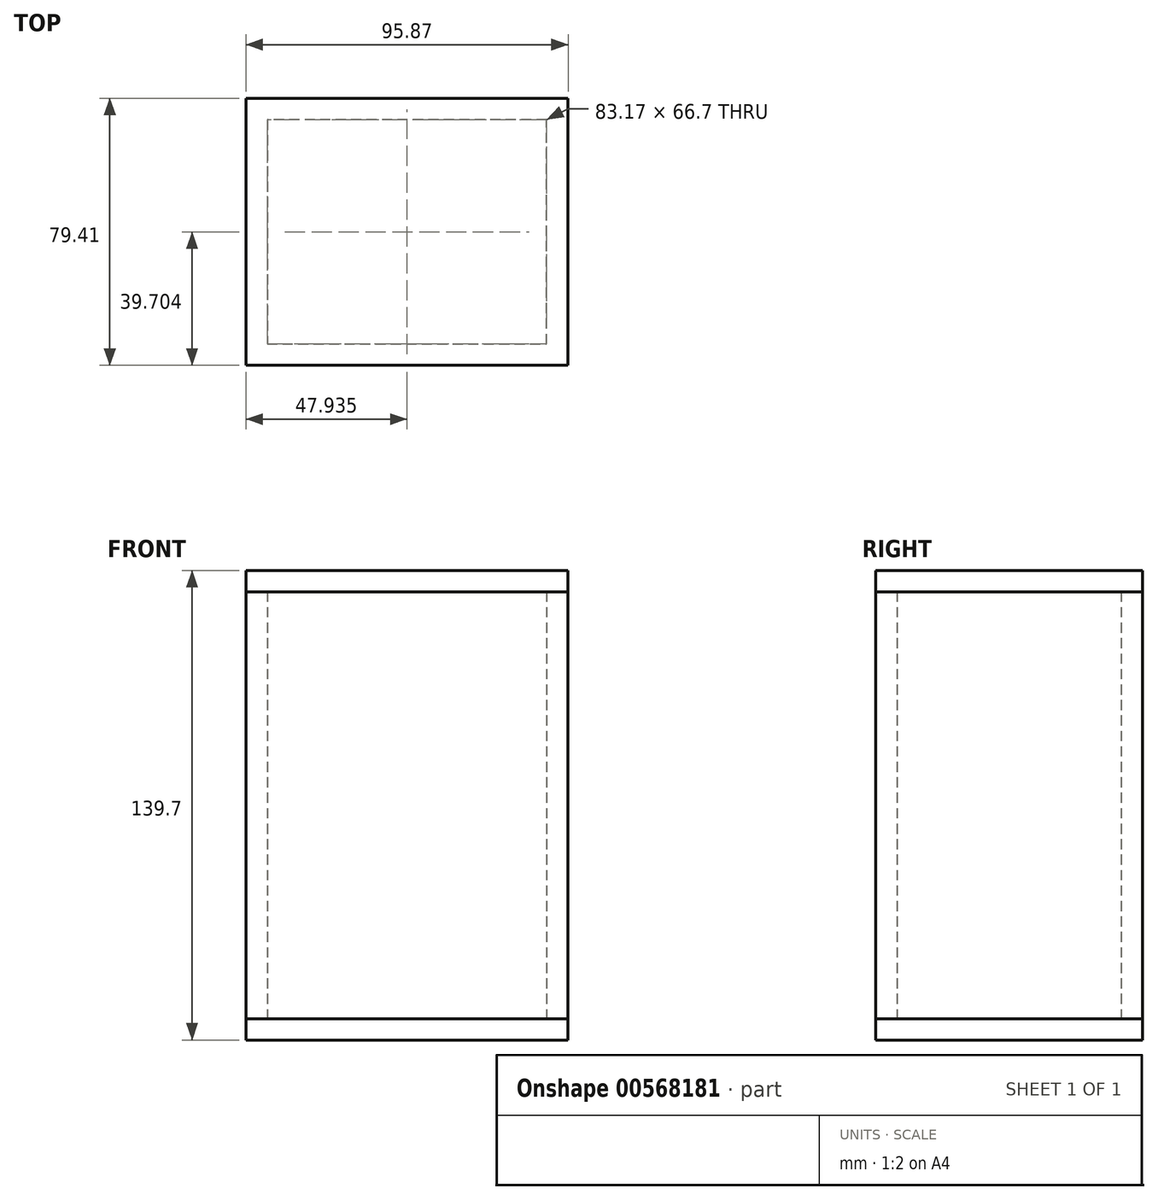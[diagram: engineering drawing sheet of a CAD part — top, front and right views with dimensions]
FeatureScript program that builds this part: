
annotation { "Feature Type Name" : "Feature", "Feature Type Description" : "" }
export const myFeature = defineFeature(function(context is Context, id is Id, definition is map)
    precondition{}
    {
        {
            var Q0;
            Q0=qCreatedBy(makeId("Top.planeOp"),FACE);
            var sketch = newSketch(context, id + "F0", { "sketchPlane" : qUnion([Q0])});
            skLineSegment(sketch, "E0.bottom", {"start": v(-45.03, -32.32) * mm, "end": v(50.84, -32.32) * mm});
            skLineSegment(sketch, "E0.top", {"start": v(-45.03, 47.09) * mm, "end": v(50.84, 47.09) * mm});
            skLineSegment(sketch, "E0.left", {"start": v(-45.03, -32.32) * mm, "end": v(-45.03, 47.09) * mm});
            skLineSegment(sketch, "E0.right", {"start": v(50.84, -32.32) * mm, "end": v(50.84, 47.09) * mm});
            skSolve(sketch);
        }
        {
            var Q0;
            Q0=makeQuery(id+"F0.imprint","IMPRINT",FACE,{"disambiguationData":[TD([[makeQuery(id+"F0.imprint","IMPRINT",EDGE,{"derivedFrom":sQuery(id+"F0.wireOp",EDGE,"E0.bottom")}),1.0]])]});
            extrude(context, id + "F1", {"entities" : qUnion([Q0]), "depth" : 6.35 * mm, "offsetDistance" : 25.4 * mm});
        }
        {
            var Q0;
            Q0=makeQuery(id+"F1.opExtrude","CAP_FACE",FACE,{"disambiguationData":[OSD([sQuery(id+"F0.wireOp",EDGE,"E0.bottom"),sQuery(id+"F0.wireOp",EDGE,"E0.top"),sQuery(id+"F0.wireOp",EDGE,"E0.left"),sQuery(id+"F0.wireOp",EDGE,"E0.right")])],"isStart":false});
            cPlane(context, id + "F2", {"entities" : qUnion([Q0]), "cplaneType" : CPlaneType.OFFSET, "offset" : 0 * mm, "width" : 152.4 * mm, "height" : 152.4 * mm});
        }
        {
            var Q0;
            Q0=qCreatedBy(id+"F2.planeOp",FACE);
            var sketch = newSketch(context, id + "F3", { "sketchPlane" : qUnion([Q0])});
            skLineSegment(sketch, "E1.bottom", {"start": v(-45.03, 47.09) * mm, "end": v(50.84, 47.09) * mm});
            skLineSegment(sketch, "E1.top", {"start": v(-45.03, -32.32) * mm, "end": v(50.84, -32.32) * mm});
            skLineSegment(sketch, "E1.left", {"start": v(-45.03, 47.09) * mm, "end": v(-45.03, -32.32) * mm});
            skLineSegment(sketch, "E1.right", {"start": v(50.84, 47.09) * mm, "end": v(50.84, -32.32) * mm});
            skLineSegment(sketch, "E2.0", {"start": v(44.49, 40.74) * mm, "end": v(-38.68, 40.74) * mm});
            skLineSegment(sketch, "E2.1", {"start": v(44.49, -25.97) * mm, "end": v(44.49, 40.74) * mm});
            skLineSegment(sketch, "E2.2", {"start": v(-38.68, -25.97) * mm, "end": v(44.49, -25.97) * mm});
            skLineSegment(sketch, "E2.3", {"start": v(-38.68, 40.74) * mm, "end": v(-38.68, -25.97) * mm});
            skSolve(sketch);
        }
        {
            var Q0;
            Q0=makeQuery(id+"F3.imprint","IMPRINT",FACE,{"disambiguationData":[TD([[makeQuery(id+"F3.imprint","IMPRINT",EDGE,{"derivedFrom":sQuery(id+"F3.wireOp",EDGE,"E1.bottom")}),-1.0]])]});
            extrude(context, id + "F4", {"entities" : qUnion([Q0]), "depth" : 127 * mm, "offsetDistance" : 25.4 * mm});
        }
        {
            var Q0;
            Q0=makeQuery(id+"F4.opExtrude","CAP_FACE",FACE,{"disambiguationData":[OSD([sQuery(id+"F3.wireOp",EDGE,"E1.bottom"),sQuery(id+"F3.wireOp",EDGE,"E1.top"),sQuery(id+"F3.wireOp",EDGE,"E1.left"),sQuery(id+"F3.wireOp",EDGE,"E1.right"),sQuery(id+"F3.wireOp",EDGE,"E2.0"),sQuery(id+"F3.wireOp",EDGE,"E2.1"),sQuery(id+"F3.wireOp",EDGE,"E2.2"),sQuery(id+"F3.wireOp",EDGE,"E2.3")])],"isStart":false});
            cPlane(context, id + "F5", {"entities" : qUnion([Q0]), "cplaneType" : CPlaneType.OFFSET, "offset" : 0 * mm, "width" : 152.4 * mm, "height" : 152.4 * mm});
        }
        {
            var Q0;
            Q0=qCreatedBy(id+"F5.planeOp",FACE);
            var sketch = newSketch(context, id + "F6", { "sketchPlane" : qUnion([Q0])});
            skLineSegment(sketch, "E3.bottom", {"start": v(-45.03, 47.09) * mm, "end": v(50.84, 47.09) * mm});
            skLineSegment(sketch, "E3.top", {"start": v(-45.03, -32.32) * mm, "end": v(50.84, -32.32) * mm});
            skLineSegment(sketch, "E3.left", {"start": v(-45.03, 47.09) * mm, "end": v(-45.03, -32.32) * mm});
            skLineSegment(sketch, "E3.right", {"start": v(50.84, 47.09) * mm, "end": v(50.84, -32.32) * mm});
            skSolve(sketch);
        }
        {
            var Q0;
            Q0=makeQuery(id+"F6.imprint","IMPRINT",FACE,{"disambiguationData":[TD([[makeQuery(id+"F6.imprint","IMPRINT",EDGE,{"derivedFrom":sQuery(id+"F6.wireOp",EDGE,"E3.bottom")}),-1.0]])]});
            extrude(context, id + "F7", {"entities" : qUnion([Q0]), "depth" : 6.35 * mm, "offsetDistance" : 25.4 * mm});
        }
    });
